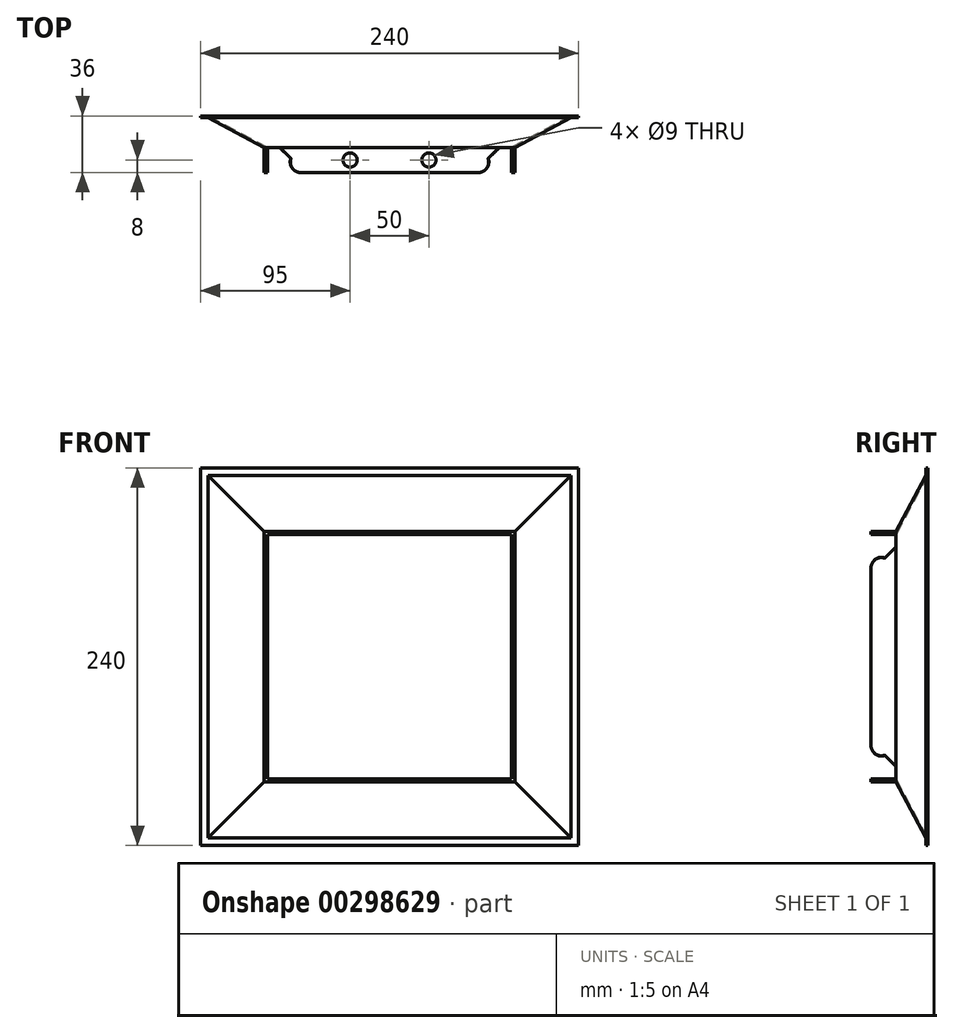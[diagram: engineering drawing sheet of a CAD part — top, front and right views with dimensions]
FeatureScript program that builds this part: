
annotation { "Feature Type Name" : "Feature", "Feature Type Description" : "" }
export const myFeature = defineFeature(function(context is Context, id is Id, definition is map)
    precondition{}
    {
        {
            var Q0;
            Q0=qCreatedBy(makeId("Front.planeOp"),FACE);
            var sketch = newSketch(context, id + "F0", { "sketchPlane" : qUnion([Q0])});
            skLineSegment(sketch, "E0.bottom", {"start": v(-120, 120) * mm, "end": v(120, 120) * mm});
            skLineSegment(sketch, "E0.top", {"start": v(-120, -120) * mm, "end": v(120, -120) * mm});
            skLineSegment(sketch, "E0.left", {"start": v(-120, 120) * mm, "end": v(-120, -120) * mm});
            skLineSegment(sketch, "E0.right", {"start": v(120, 120) * mm, "end": v(120, -120) * mm});
            skLineSegment(sketch, "E1.bottom", {"start": v(115, -115) * mm, "end": v(-115, -115) * mm});
            skLineSegment(sketch, "E1.top", {"start": v(115, 115) * mm, "end": v(-115, 115) * mm});
            skLineSegment(sketch, "E1.left", {"start": v(115, -115) * mm, "end": v(115, 115) * mm});
            skLineSegment(sketch, "E1.right", {"start": v(-115, -115) * mm, "end": v(-115, 115) * mm});
            skPoint(sketch, "E1.middle", {"position": v(0, 0) * mm});
            skSolve(sketch);
        }
        {
            var Q0;
            Q0=makeQuery(id+"F0.imprint","IMPRINT",FACE,{"disambiguationData":[TD([[makeQuery(id+"F0.imprint","IMPRINT",EDGE,{"derivedFrom":sQuery(id+"F0.wireOp",EDGE,"E0.bottom")}),-1.0]])]});
            cPlane(context, id + "F1", {"entities" : qUnion([Q0]), "cplaneType" : CPlaneType.OFFSET, "offset" : 20 * mm, "width" : 150 * mm, "height" : 150 * mm});
        }
        {
            var Q0;
            Q0=qCreatedBy(id+"F1.planeOp",FACE);
            var sketch = newSketch(context, id + "F2", { "sketchPlane" : qUnion([Q0])});
            skLineSegment(sketch, "E2.bottom", {"start": v(77.5, -77.5) * mm, "end": v(-77.5, -77.5) * mm});
            skLineSegment(sketch, "E2.top", {"start": v(77.5, 77.5) * mm, "end": v(-77.5, 77.5) * mm});
            skLineSegment(sketch, "E2.left", {"start": v(77.5, -77.5) * mm, "end": v(77.5, 77.5) * mm});
            skLineSegment(sketch, "E2.right", {"start": v(-77.5, -77.5) * mm, "end": v(-77.5, 77.5) * mm});
            skPoint(sketch, "E2.middle", {"position": v(0, 0) * mm});
            skSolve(sketch);
        }
        {
            var Q0;
            Q0=makeQuery(id+"F0.imprint","IMPRINT",FACE,{"disambiguationData":[TD([[makeQuery(id+"F0.imprint","IMPRINT",EDGE,{"derivedFrom":sQuery(id+"F0.wireOp",EDGE,"E1.bottom")}),-1.0]])]});
            var Q1;
            Q1=makeQuery(id+"F2.imprint","IMPRINT",FACE,{"disambiguationData":[TD([[makeQuery(id+"F2.imprint","IMPRINT",EDGE,{"derivedFrom":sQuery(id+"F2.wireOp",EDGE,"E2.bottom")}),-1.0]])]});
            loft(context, id + "F3", {"sheetProfilesArray" : [{ "sheetProfileEntities" : qUnion([Q0]) }, { "sheetProfileEntities" : qUnion([Q1]) }]});
        }
        {
            var Q0;
            Q0=makeQuery(id+"F3.opLoft","CAP_FACE",FACE,{"disambiguationData":[OSD([makeQuery(id+"F2.imprint","IMPRINT",FACE,{"disambiguationData":[TD([[makeQuery(id+"F2.imprint","IMPRINT",EDGE,{"derivedFrom":sQuery(id+"F2.wireOp",EDGE,"E2.bottom")}),-1.0]])]})])],"isStart":true});
            var Q1;
            Q1=makeQuery(id+"F3.opLoft","CAP_FACE",FACE,{"disambiguationData":[OSD([makeQuery(id+"F0.imprint","IMPRINT",FACE,{"disambiguationData":[TD([[makeQuery(id+"F0.imprint","IMPRINT",EDGE,{"derivedFrom":sQuery(id+"F0.wireOp",EDGE,"E1.bottom")}),-1.0]])]})])],"isStart":true});
            shell(context, id + "F4", {"entities" : qUnion([Q0, Q1]), "thickness" : 1 * mm, "oppositeDirection" : true});
        }
        {
            var Q0;
            Q0=makeQuery(id+"F0.imprint","IMPRINT",FACE,{"disambiguationData":[TD([[makeQuery(id+"F0.imprint","IMPRINT",EDGE,{"derivedFrom":sQuery(id+"F0.wireOp",EDGE,"E0.bottom")}),-1.0]])]});
            extrude(context, id + "F5", {"entities" : qUnion([Q0]), "operationType" : NewBodyOperationType.ADD, "depth" : 1 * mm});
        }
        {
            var Q0;
            Q0=makeQuery(id+"F3.opLoft","CAP_FACE",FACE,{"disambiguationData":[OSD([makeQuery(id+"F2.imprint","IMPRINT",FACE,{"disambiguationData":[TD([[makeQuery(id+"F2.imprint","IMPRINT",EDGE,{"derivedFrom":sQuery(id+"F2.wireOp",EDGE,"E2.bottom")}),-1.0]])]})])],"isStart":true});
            var sketch = newSketch(context, id + "F6", { "sketchPlane" : qUnion([Q0])});
            skLineSegment(sketch, "E3.0", {"start": v(-77.5, -77.5) * mm, "end": v(77.5, -77.5) * mm});
            skLineSegment(sketch, "E4.0", {"start": v(77.5, -77.5) * mm, "end": v(77.5, 77.5) * mm});
            skLineSegment(sketch, "E5.0", {"start": v(79.62, -79.62) * mm, "end": v(79.62, 79.62) * mm});
            skLineSegment(sketch, "E6.0", {"start": v(79.62, 79.63) * mm, "end": v(-79.62, 79.62) * mm});
            skLineSegment(sketch, "E7.0", {"start": v(77.5, 77.5) * mm, "end": v(-77.5, 77.5) * mm});
            skLineSegment(sketch, "E8.0", {"start": v(-79.62, 79.62) * mm, "end": v(-79.62, -79.63) * mm});
            skLineSegment(sketch, "E9.0", {"start": v(-77.5, 77.5) * mm, "end": v(-77.5, -77.5) * mm});
            skLineSegment(sketch, "E10.0", {"start": v(-79.62, -79.63) * mm, "end": v(79.62, -79.63) * mm});
            skSolve(sketch);
        }
        {
            var Q0;
            Q0=qSketchRegion(id+"F6",true);
            extrude(context, id + "F7", {"entities" : qUnion([Q0]), "operationType" : NewBodyOperationType.ADD, "depth" : 16 * mm});
        }
        {
            var Q0;
            Q0=makeQuery(id+"F7.opExtrude","SWEPT_FACE",FACE,{"disambiguationData":[OSD([sQuery(id+"F6.wireOp",EDGE,"E6.0")])]});
            var sketch = newSketch(context, id + "F8", { "sketchPlane" : qUnion([Q0])});
            skLineSegment(sketch, "E11", {"start": v(79.62, -20) * mm, "end": v(69.62, -20) * mm});
            skLineSegment(sketch, "E12", {"start": v(69.62, -20) * mm, "end": v(62.55, -27.07) * mm});
            skArc(sketch, "E13", {"start": v(56.24, -36) * mm, "mid": v(61.7, -33.17) * mm, "end": v(62.55, -27.07) * mm});
            skLineSegment(sketch, "E14", {"start": v(79.62, -20) * mm, "end": v(79.62, -36) * mm});
            skLineSegment(sketch, "E15", {"start": v(56.24, -36) * mm, "end": v(79.62, -36) * mm});
            skLineSegment(sketch, "E16", {"start": v(-79.62, -20) * mm, "end": v(-69.62, -20) * mm});
            skLineSegment(sketch, "E17", {"start": v(-69.62, -20) * mm, "end": v(-62.55, -27.07) * mm});
            skArc(sketch, "E18", {"start": v(-62.55, -27.07) * mm, "mid": v(-61.7, -33.17) * mm, "end": v(-56.24, -36) * mm});
            skLineSegment(sketch, "E19", {"start": v(-56.24, -36) * mm, "end": v(-79.62, -36) * mm});
            skLineSegment(sketch, "E20", {"start": v(-79.62, -36) * mm, "end": v(-79.62, -20) * mm});
            skSolve(sketch);
        }
        {
            var Q0;
            Q0=makeQuery(id+"F8.imprint","IMPRINT",FACE,{"disambiguationData":[TD([[makeQuery(id+"F8.imprint","IMPRINT",EDGE,{"derivedFrom":sQuery(id+"F8.wireOp",EDGE,"E11")}),1.0]])]});
            var Q1;
            Q1=sQuery(id+"F8.wireOp",EDGE,"E14");
            revolve(context, id + "F9", {"operationType" : NewBodyOperationType.REMOVE, "entities" : qUnion([Q0]), "axis" : qUnion([Q1]), "revolveType" : RevolveType.FULL, "oppositeDirection" : true});
        }
        {
            var Q0;
            Q0=makeQuery(id+"F8.imprint","IMPRINT",FACE,{"disambiguationData":[TD([[makeQuery(id+"F8.imprint","IMPRINT",EDGE,{"derivedFrom":sQuery(id+"F8.wireOp",EDGE,"E16")}),1.0]])]});
            var Q1;
            Q1=sQuery(id+"F8.wireOp",EDGE,"E20");
            revolve(context, id + "F10", {"operationType" : NewBodyOperationType.REMOVE, "entities" : qUnion([Q0]), "axis" : qUnion([Q1]), "revolveType" : RevolveType.FULL, "oppositeDirection" : true});
        }
        {
            var Q0;
            Q0=makeQuery(id+"F7.opExtrude","SWEPT_FACE",FACE,{"disambiguationData":[OSD([sQuery(id+"F6.wireOp",EDGE,"E10.0")])]});
            var sketch = newSketch(context, id + "F11", { "sketchPlane" : qUnion([Q0])});
            skLineSegment(sketch, "E21.0", {"start": v(-56.24, 36) * mm, "end": v(-79.62, 36) * mm});
            skArc(sketch, "E22.0", {"start": v(-62.55, 27.07) * mm, "mid": v(-61.7, 33.17) * mm, "end": v(-56.24, 36) * mm});
            skLineSegment(sketch, "E22.1", {"start": v(-79.63, 36) * mm, "end": v(-79.63, 20) * mm});
            skLineSegment(sketch, "E22.2", {"start": v(-69.63, 20) * mm, "end": v(-62.55, 27.07) * mm});
            skLineSegment(sketch, "E23.0", {"start": v(-79.62, 20) * mm, "end": v(-69.63, 20) * mm});
            skLineSegment(sketch, "E24.0", {"start": v(56.24, 36) * mm, "end": v(79.62, 36) * mm});
            skLineSegment(sketch, "E25.0", {"start": v(79.62, 20) * mm, "end": v(79.62, 36) * mm});
            skArc(sketch, "E26.0", {"start": v(56.24, 36) * mm, "mid": v(61.7, 33.17) * mm, "end": v(62.55, 27.07) * mm});
            skLineSegment(sketch, "E27.0", {"start": v(69.62, 20) * mm, "end": v(62.55, 27.07) * mm});
            skLineSegment(sketch, "E28.0", {"start": v(79.62, 20) * mm, "end": v(69.62, 20) * mm});
            skSolve(sketch);
        }
        {
            var Q0;
            Q0=makeQuery(id+"F11.imprint","IMPRINT",FACE,{"disambiguationData":[TD([[makeQuery(id+"F11.imprint","IMPRINT",EDGE,{"derivedFrom":sQuery(id+"F11.wireOp",EDGE,"E24.0")}),-1.0]])]});
            var Q1;
            Q1=sQuery(id+"F11.wireOp",EDGE,"E25.0");
            revolve(context, id + "F12", {"operationType" : NewBodyOperationType.REMOVE, "entities" : qUnion([Q0]), "axis" : qUnion([Q1]), "revolveType" : RevolveType.FULL, "oppositeDirection" : true});
        }
        {
            var Q0;
            Q0=makeQuery(id+"F11.imprint","IMPRINT",FACE,{"disambiguationData":[TD([[makeQuery(id+"F11.imprint","IMPRINT",EDGE,{"derivedFrom":sQuery(id+"F11.wireOp",EDGE,"E21.0")}),-1.0]])]});
            var Q1;
            Q1=sQuery(id+"F11.wireOp",EDGE,"E22.1");
            revolve(context, id + "F13", {"operationType" : NewBodyOperationType.REMOVE, "entities" : qUnion([Q0]), "axis" : qUnion([Q1]), "revolveType" : RevolveType.FULL, "oppositeDirection" : true});
        }
        {
            var Q0;
            Q0=makeQuery(id+"F7.opExtrude","SWEPT_FACE",FACE,{"disambiguationData":[OSD([sQuery(id+"F6.wireOp",EDGE,"E10.0")])]});
            var sketch = newSketch(context, id + "F14", { "sketchPlane" : qUnion([Q0])});
            skLineSegment(sketch, "E29", {"start": v(-113.65, 28) * mm, "end": v(128.14, 28) * mm, "construction": true});
            skCircle(sketch, "E30", {"center": v(-25, 28) * mm, "radius": 4.5 * mm});
            skCircle(sketch, "E31", {"center": v(25, 28) * mm, "radius": 4.5 * mm});
            skSolve(sketch);
        }
        {
            var Q0;
            Q0=makeQuery(id+"F14.imprint","IMPRINT",FACE,{"disambiguationData":[TD([[makeQuery(id+"F14.imprint","IMPRINT",EDGE,{"derivedFrom":sQuery(id+"F14.wireOp",EDGE,"E30")}),1.0]])]});
            var Q1;
            Q1=makeQuery(id+"F14.imprint","IMPRINT",FACE,{"disambiguationData":[TD([[makeQuery(id+"F14.imprint","IMPRINT",EDGE,{"derivedFrom":sQuery(id+"F14.wireOp",EDGE,"E31")}),1.0]])]});
            extrude(context, id + "F15", {"entities" : qUnion([Q0, Q1]), "operationType" : NewBodyOperationType.REMOVE, "endBound" : BoundingType.THROUGH_ALL, "oppositeDirection" : true, "depth" : 25 * mm});
        }
    });
